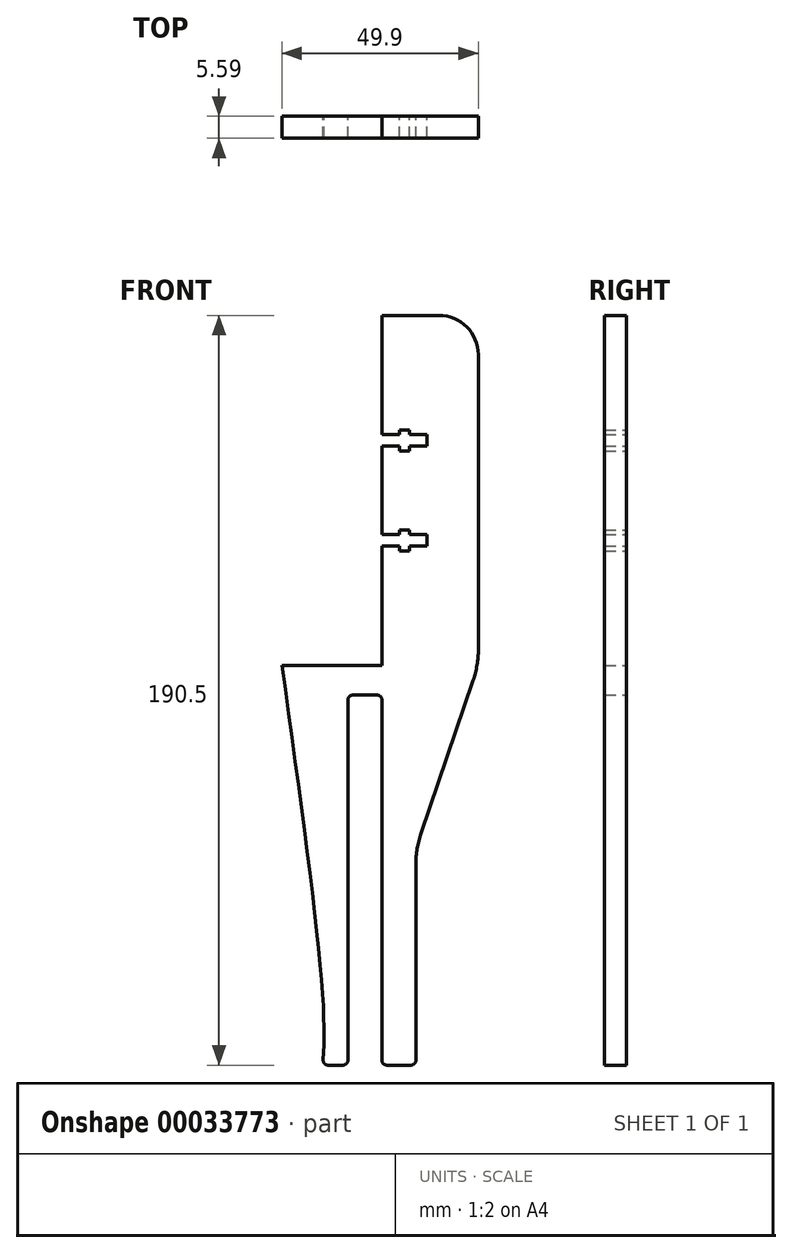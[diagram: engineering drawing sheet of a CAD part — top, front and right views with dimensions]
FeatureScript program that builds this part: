
annotation { "Feature Type Name" : "Feature", "Feature Type Description" : "" }
export const myFeature = defineFeature(function(context is Context, id is Id, definition is map)
    precondition{}
    {
        {
            var Q0;
            Q0=qCreatedBy(makeId("Front.planeOp"),FACE);
            var sketch = newSketch(context, id + "F0", { "sketchPlane" : qUnion([Q0])});
            skLineSegment(sketch, "E0", {"start": v(-88.5, 0) * mm, "end": v(97.9, 0) * mm, "construction": true});
            skLineSegment(sketch, "E1", {"start": v(0, 0) * mm, "end": v(0, -84.86) * mm, "construction": true});
            skLineSegment(sketch, "E2.0", {"start": v(8.64, 7.28) * mm, "end": v(8.64, 0) * mm, "construction": true});
            skLineSegment(sketch, "E3.0", {"start": v(-88.5, 57.15) * mm, "end": v(97.9, 57.15) * mm, "construction": true});
            skLineSegment(sketch, "E4.0", {"start": v(-88.5, 31.75) * mm, "end": v(97.9, 31.75) * mm, "construction": true});
            skLineSegment(sketch, "E5", {"start": v(0, 88.9) * mm, "end": v(0, 58.61) * mm});
            skLineSegment(sketch, "E6", {"start": v(0, 57.15) * mm, "end": v(0, 31.75) * mm, "construction": true});
            skLineSegment(sketch, "E7", {"start": v(0, 31.75) * mm, "end": v(0, 0) * mm, "construction": true});
            skLineSegment(sketch, "E8", {"start": v(0, 44.45) * mm, "end": v(118.24, 44.45) * mm, "construction": true});
            skLineSegment(sketch, "E9.0", {"start": v(-88.5, 55.69) * mm, "end": v(97.9, 55.69) * mm, "construction": true});
            skLineSegment(sketch, "E10.0", {"start": v(-88.5, 54.46) * mm, "end": v(97.9, 54.46) * mm, "construction": true});
            skLineSegment(sketch, "E11.MirrorCS", {"start": v(-88.5, 58.61) * mm, "end": v(97.9, 58.61) * mm, "construction": true});
            skLineSegment(sketch, "E12.MirrorCS", {"start": v(-88.5, 59.84) * mm, "end": v(97.9, 59.84) * mm, "construction": true});
            skLineSegment(sketch, "E13", {"start": v(11.43, 44.45) * mm, "end": v(11.43, 88.9) * mm, "construction": true});
            skLineSegment(sketch, "E14.0", {"start": v(-93.34, 88.9) * mm, "end": v(0, 88.9) * mm, "construction": true});
            skLineSegment(sketch, "E15", {"start": v(0, 88.9) * mm, "end": v(11.43, 88.9) * mm, "construction": true});
            skLineSegment(sketch, "E16", {"start": v(5.71, 88.9) * mm, "end": v(5.71, 44.45) * mm, "construction": true});
            skLineSegment(sketch, "E17.0", {"start": v(4.44, 88.9) * mm, "end": v(4.45, 44.45) * mm, "construction": true});
            skLineSegment(sketch, "E18.MirrorCS", {"start": v(6.99, 88.9) * mm, "end": v(6.98, 44.45) * mm, "construction": true});
            skLineSegment(sketch, "E19", {"start": v(0, 58.61) * mm, "end": v(4.44, 58.61) * mm});
            skLineSegment(sketch, "E20", {"start": v(4.44, 58.61) * mm, "end": v(4.44, 59.84) * mm});
            skLineSegment(sketch, "E21", {"start": v(4.44, 59.84) * mm, "end": v(6.98, 59.84) * mm});
            skLineSegment(sketch, "E22", {"start": v(6.98, 59.84) * mm, "end": v(6.98, 58.61) * mm});
            skLineSegment(sketch, "E23", {"start": v(6.98, 58.61) * mm, "end": v(11.43, 58.61) * mm});
            skLineSegment(sketch, "E24", {"start": v(11.43, 58.61) * mm, "end": v(11.43, 55.69) * mm});
            skLineSegment(sketch, "E25", {"start": v(11.43, 55.69) * mm, "end": v(6.98, 55.69) * mm});
            skLineSegment(sketch, "E26", {"start": v(6.98, 55.69) * mm, "end": v(6.98, 54.46) * mm});
            skLineSegment(sketch, "E27", {"start": v(6.98, 54.46) * mm, "end": v(4.44, 54.46) * mm});
            skLineSegment(sketch, "E28", {"start": v(4.44, 54.46) * mm, "end": v(4.44, 55.69) * mm});
            skLineSegment(sketch, "E29", {"start": v(4.44, 55.69) * mm, "end": v(0, 55.69) * mm});
            skLineSegment(sketch, "E30.MirrorCS", {"start": v(0, 30.29) * mm, "end": v(4.44, 30.29) * mm});
            skLineSegment(sketch, "E31.MirrorCS", {"start": v(4.44, 30.29) * mm, "end": v(4.44, 29.06) * mm});
            skLineSegment(sketch, "E32.MirrorCS", {"start": v(4.44, 29.06) * mm, "end": v(6.98, 29.06) * mm});
            skLineSegment(sketch, "E33.MirrorCS", {"start": v(6.98, 29.06) * mm, "end": v(6.98, 30.29) * mm});
            skLineSegment(sketch, "E34.MirrorCS", {"start": v(6.98, 30.29) * mm, "end": v(11.43, 30.29) * mm});
            skLineSegment(sketch, "E35.MirrorCS", {"start": v(11.43, 30.29) * mm, "end": v(11.43, 33.21) * mm});
            skLineSegment(sketch, "E36.MirrorCS", {"start": v(11.43, 33.21) * mm, "end": v(6.98, 33.21) * mm});
            skLineSegment(sketch, "E37.MirrorCS", {"start": v(6.98, 33.21) * mm, "end": v(6.98, 34.44) * mm});
            skLineSegment(sketch, "E38.MirrorCS", {"start": v(6.98, 34.44) * mm, "end": v(4.44, 34.44) * mm});
            skLineSegment(sketch, "E39.MirrorCS", {"start": v(4.44, 34.44) * mm, "end": v(4.44, 33.21) * mm});
            skLineSegment(sketch, "E40.MirrorCS", {"start": v(4.44, 33.21) * mm, "end": v(0, 33.21) * mm});
            skLineSegment(sketch, "E41", {"start": v(0, 0) * mm, "end": v(-25.4, 0) * mm});
            skLineSegment(sketch, "E42", {"start": v(8.64, -50.59) * mm, "end": v(8.64, -100.32) * mm});
            skLineSegment(sketch, "E43.0", {"start": v(-8.64, 0) * mm, "end": v(-8.64, -84.86) * mm, "construction": true});
            skLineSegment(sketch, "E44.0", {"start": v(-14.99, 0) * mm, "end": v(-14.99, -84.86) * mm, "construction": true});
            skFitSpline(sketch, "E45", {"points": [v(-25.4, 0) * mm, v(-14.99, -84.86) * mm, v(-14.99, -101.6) * mm], "startDerivative": vector(20.23, -145.92) * mm, "endDerivative": vector(-2.3, -44.17) * mm});
            skLineSegment(sketch, "E46", {"start": v(-13.64, -101.6) * mm, "end": v(-9.91, -101.6) * mm});
            skLineSegment(sketch, "E47", {"start": v(-8.64, -100.32) * mm, "end": v(-8.64, -8.82) * mm});
            skLineSegment(sketch, "E48", {"start": v(-7.36, -7.54) * mm, "end": v(-1.28, -7.54) * mm});
            skLineSegment(sketch, "E49", {"start": v(0, -8.82) * mm, "end": v(0, -100.32) * mm});
            skLineSegment(sketch, "E50", {"start": v(1.28, -101.6) * mm, "end": v(7.36, -101.6) * mm});
            skArc(sketch, "E51.filletArc", {"start": v(-14.92, -100.26) * mm, "mid": v(-14.57, -101.2) * mm, "end": v(-13.64, -101.6) * mm});
            skPoint(sketch, "E52.visualSharp", {"position": v(-8.64, -101.6) * mm});
            skArc(sketch, "E52.filletArc", {"start": v(-9.91, -101.6) * mm, "mid": v(-9.01, -101.23) * mm, "end": v(-8.64, -100.32) * mm});
            skPoint(sketch, "E53.visualSharp", {"position": v(0, -101.6) * mm});
            skArc(sketch, "E53.filletArc", {"start": v(0, -100.32) * mm, "mid": v(0.37, -101.23) * mm, "end": v(1.28, -101.6) * mm});
            skPoint(sketch, "E54.visualSharp", {"position": v(8.64, -101.6) * mm});
            skArc(sketch, "E54.filletArc", {"start": v(7.36, -101.6) * mm, "mid": v(8.26, -101.23) * mm, "end": v(8.64, -100.32) * mm});
            skPoint(sketch, "E55.visualSharp", {"position": v(-8.64, -7.54) * mm});
            skArc(sketch, "E55.filletArc", {"start": v(-7.36, -7.54) * mm, "mid": v(-8.26, -7.92) * mm, "end": v(-8.64, -8.82) * mm});
            skPoint(sketch, "E56.visualSharp", {"position": v(0, -7.54) * mm});
            skArc(sketch, "E56.filletArc", {"start": v(0, -8.82) * mm, "mid": v(-0.37, -7.92) * mm, "end": v(-1.28, -7.54) * mm});
            skPoint(sketch, "E57.visualSharp", {"position": v(8.64, 0) * mm});
            skLineSegment(sketch, "E58.trimOffspring", {"start": v(0, 30.29) * mm, "end": v(0, 0) * mm});
            skLineSegment(sketch, "E59.trimOffspring", {"start": v(0, 55.69) * mm, "end": v(0, 33.21) * mm});
            skLineSegment(sketch, "E60", {"start": v(0, 88.9) * mm, "end": v(14.5, 88.9) * mm});
            skLineSegment(sketch, "E61", {"start": v(24.5, 78.9) * mm, "end": v(24.5, 4.06) * mm});
            skLineSegment(sketch, "E62", {"start": v(23.19, -3.84) * mm, "end": v(9.95, -42.68) * mm});
            skLineSegment(sketch, "E63.trimOffspring", {"start": v(8.64, -46.52) * mm, "end": v(8.64, -84.86) * mm, "construction": true});
            skPoint(sketch, "E64.visualSharp", {"position": v(8.64, -46.52) * mm});
            skArc(sketch, "E64.filletArc", {"start": v(9.95, -42.68) * mm, "mid": v(8.97, -46.58) * mm, "end": v(8.64, -50.59) * mm});
            skPoint(sketch, "E65.visualSharp", {"position": v(24.5, 0) * mm});
            skArc(sketch, "E65.filletArc", {"start": v(23.19, -3.84) * mm, "mid": v(24.17, 0.05) * mm, "end": v(24.5, 4.06) * mm});
            skPoint(sketch, "E66.visualSharp", {"position": v(24.5, 88.9) * mm});
            skArc(sketch, "E66.filletArc", {"start": v(24.5, 78.9) * mm, "mid": v(21.57, 85.97) * mm, "end": v(14.5, 88.9) * mm});
            skLineSegment(sketch, "E67", {"start": v(-13.64, -101.6) * mm, "end": v(-47.13, -101.6) * mm, "construction": true});
            skSolve(sketch);
        }
        {
            var Q0;
            Q0=makeQuery(id+"F0.imprint","IMPRINT",FACE,{"disambiguationData":[TD([[makeQuery(id+"F0.imprint","IMPRINT",EDGE,{"derivedFrom":sQuery(id+"F0.wireOp",EDGE,"E19")}),1.0]])]});
            extrude(context, id + "F1", {"entities" : qUnion([Q0]), "offsetDistance" : 25 * mm, "depth" : 5.6 * mm});
        }
    });
